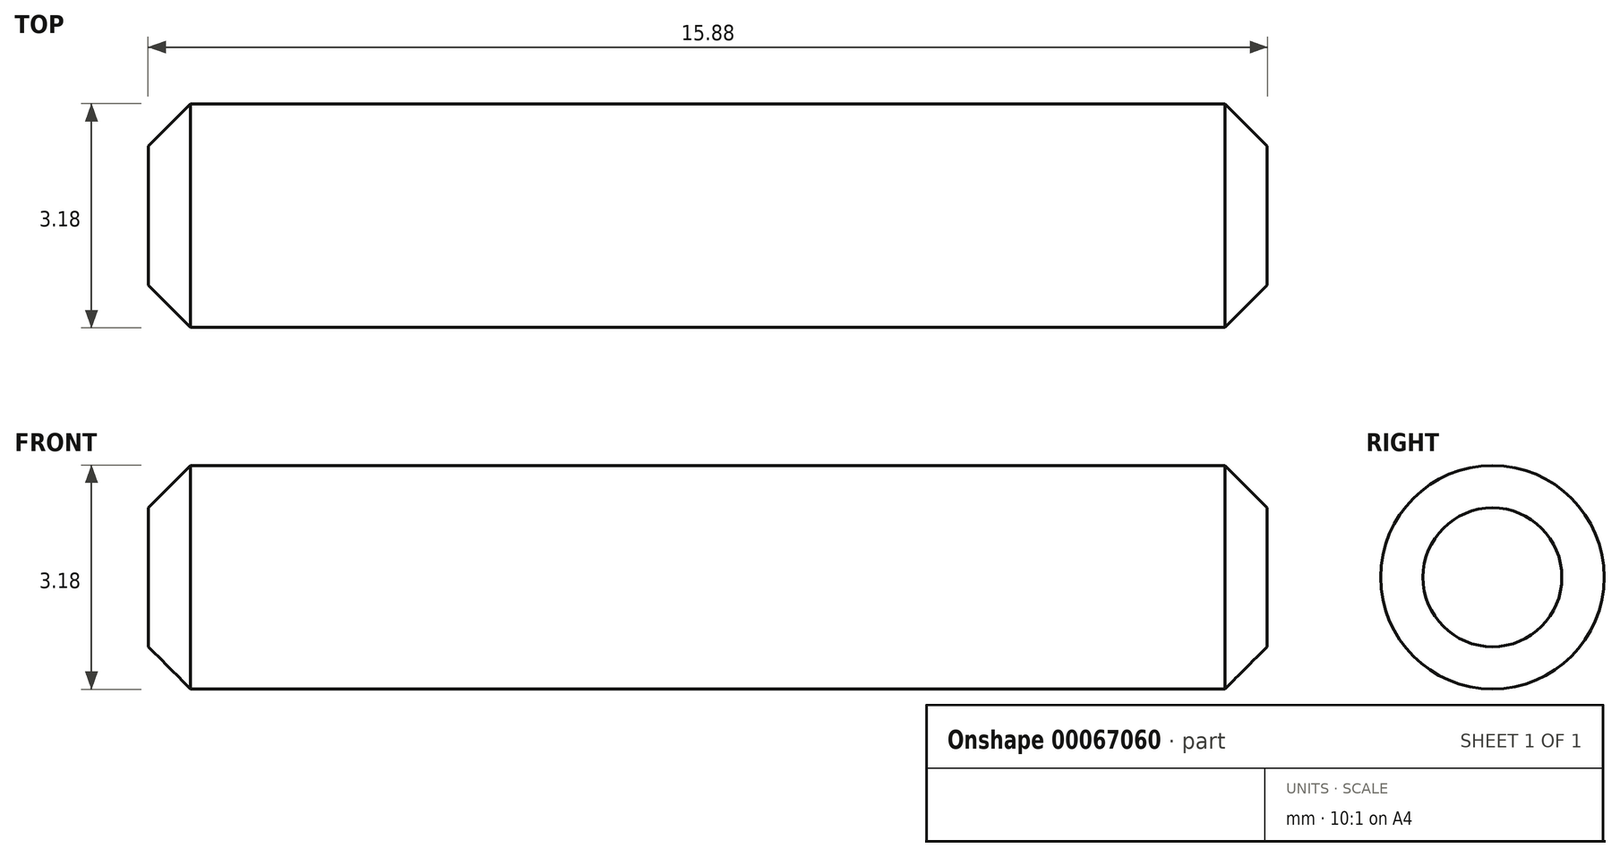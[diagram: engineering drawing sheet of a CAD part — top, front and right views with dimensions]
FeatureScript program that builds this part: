
annotation { "Feature Type Name" : "Feature", "Feature Type Description" : "" }
export const myFeature = defineFeature(function(context is Context, id is Id, definition is map)
    precondition{}
    {
        {
            var Q0;
            Q0=qCreatedBy(makeId("Right.planeOp"),FACE);
            var sketch = newSketch(context, id + "F0", { "sketchPlane" : qUnion([Q0])});
            skCircle(sketch, "E0", {"center": v(0, 0) * mm, "radius": 1.59 * mm});
            skSolve(sketch);
        }
        {
            var Q0;
            Q0=qSketchRegion(id+"F0",true);
            extrude(context, id + "F1", {"entities" : qUnion([Q0]), "endBound" : BoundingType.SYMMETRIC, "depth" : 15.87 * mm});
        }
        {
            var Q0;
            Q0=makeQuery(id+"F1.opExtrude","SWEPT_FACE",FACE,{"disambiguationData":[OSD([sQuery(id+"F0.wireOp",EDGE,"E0")])]});
            chamfer(context, id + "F2", {"entities" : qUnion([Q0]), "width" : 0.6 * mm, "tangentPropagation" : true});
        }
    });
